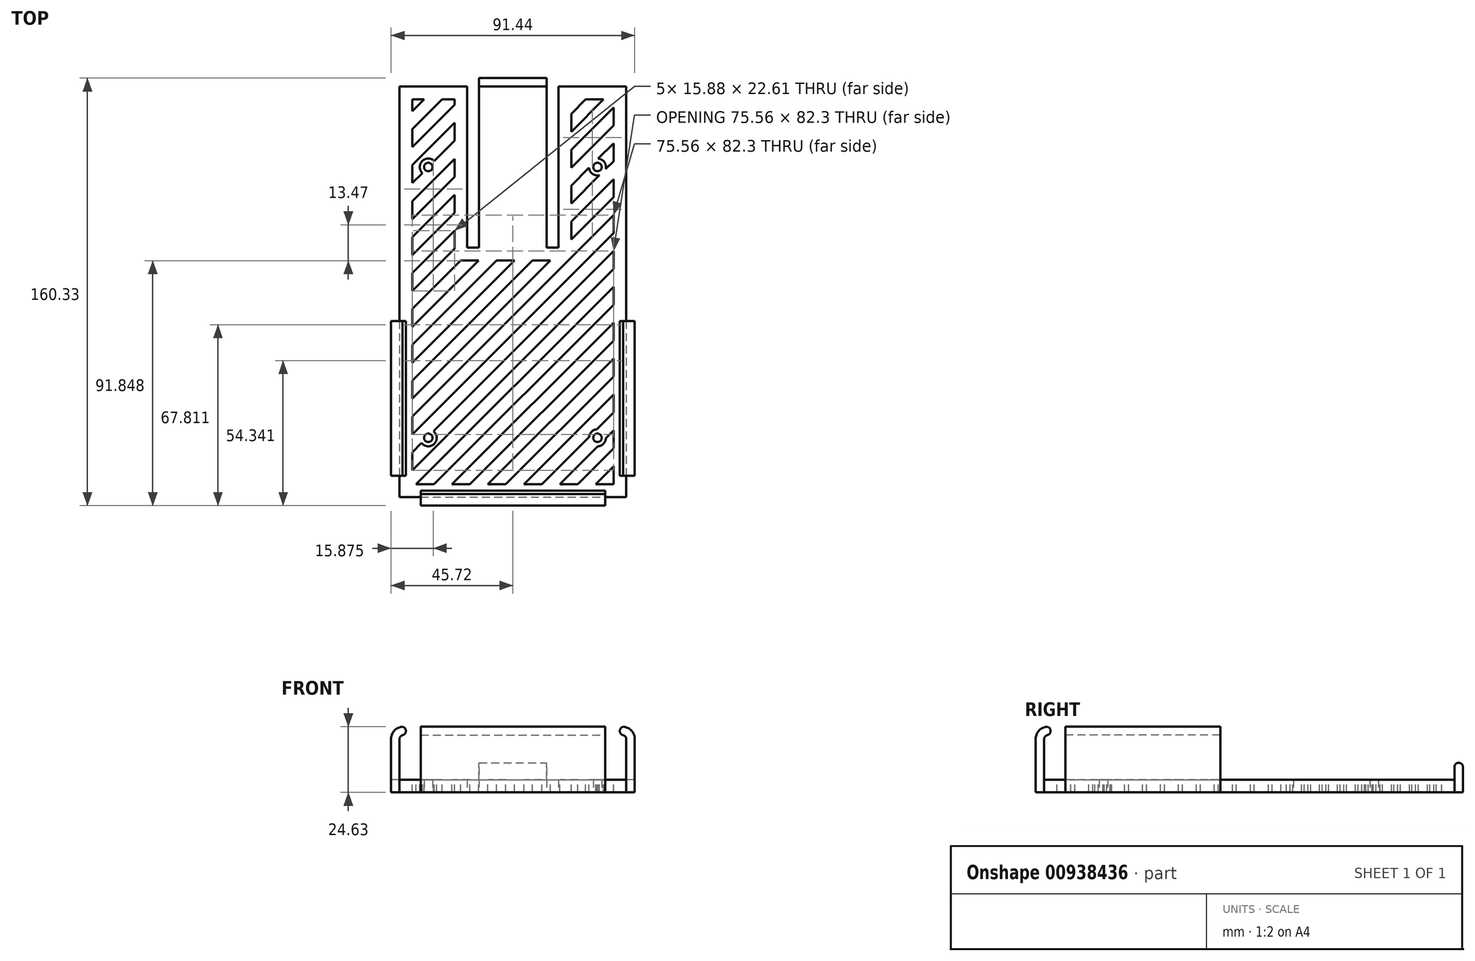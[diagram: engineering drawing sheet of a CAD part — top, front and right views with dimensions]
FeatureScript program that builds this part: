
annotation { "Feature Type Name" : "Feature", "Feature Type Description" : "" }
export const myFeature = defineFeature(function(context is Context, id is Id, definition is map)
    precondition{}
    {
        {
            var Q0;
            Q0=qCreatedBy(makeId("Top.planeOp"),FACE);
            var sketch = newSketch(context, id + "F0", { "sketchPlane" : qUnion([Q0])});
            skLineSegment(sketch, "E0.bottom", {"start": v(-42.54, 87.9) * mm, "end": v(-17.14, 87.9) * mm});
            skLineSegment(sketch, "E0.left", {"start": v(-42.54, 87.9) * mm, "end": v(-42.55, 0) * mm});
            skLineSegment(sketch, "E0.right", {"start": v(42.55, 87.9) * mm, "end": v(42.55, 0) * mm});
            skLineSegment(sketch, "E1", {"start": v(-42.55, 0) * mm, "end": v(-45.72, 0) * mm});
            skLineSegment(sketch, "E2", {"start": v(-45.72, 0) * mm, "end": v(-45.72, -58.15) * mm});
            skLineSegment(sketch, "E3", {"start": v(-45.72, -58.15) * mm, "end": v(-42.54, -58.15) * mm});
            skLineSegment(sketch, "E4", {"start": v(-34.6, -66.09) * mm, "end": v(-34.6, -69.26) * mm});
            skLineSegment(sketch, "E5", {"start": v(-34.6, -69.26) * mm, "end": v(34.6, -69.26) * mm});
            skLineSegment(sketch, "E6", {"start": v(34.6, -69.26) * mm, "end": v(34.6, -66.09) * mm});
            skLineSegment(sketch, "E7", {"start": v(42.54, -58.15) * mm, "end": v(45.72, -58.15) * mm});
            skLineSegment(sketch, "E8", {"start": v(45.72, -58.15) * mm, "end": v(45.72, 0) * mm});
            skLineSegment(sketch, "E9", {"start": v(45.72, 0) * mm, "end": v(42.55, 0) * mm});
            skLineSegment(sketch, "E10", {"start": v(-17.14, 87.9) * mm, "end": v(-17.15, 27.49) * mm});
            skLineSegment(sketch, "E11", {"start": v(-17.15, 27.49) * mm, "end": v(-12.7, 27.49) * mm});
            skLineSegment(sketch, "E12", {"start": v(17.15, 27.49) * mm, "end": v(17.15, 87.9) * mm});
            skLineSegment(sketch, "E13.trimOffspring", {"start": v(17.14, 87.9) * mm, "end": v(42.54, 87.9) * mm});
            skLineSegment(sketch, "E14", {"start": v(-12.7, 27.49) * mm, "end": v(-12.7, 91.07) * mm});
            skLineSegment(sketch, "E15", {"start": v(-12.7, 91.07) * mm, "end": v(12.7, 91.07) * mm});
            skLineSegment(sketch, "E16", {"start": v(12.7, 91.07) * mm, "end": v(12.7, 27.49) * mm});
            skLineSegment(sketch, "E17.trimOffspring", {"start": v(12.7, 27.49) * mm, "end": v(17.15, 27.49) * mm});
            skCircle(sketch, "E18", {"center": v(-31.75, -43.86) * mm, "radius": 1.59 * mm});
            skCircle(sketch, "E19", {"center": v(31.75, -43.86) * mm, "radius": 1.59 * mm});
            skCircle(sketch, "E20", {"center": v(31.75, 57.74) * mm, "radius": 1.59 * mm});
            skCircle(sketch, "E21", {"center": v(-31.75, 57.74) * mm, "radius": 1.59 * mm});
            skLineSegment(sketch, "E22", {"start": v(-42.54, -58.15) * mm, "end": v(-42.54, -66.09) * mm});
            skLineSegment(sketch, "E23", {"start": v(-42.54, -66.09) * mm, "end": v(-34.6, -66.09) * mm});
            skLineSegment(sketch, "E24", {"start": v(42.54, -58.15) * mm, "end": v(42.54, -66.09) * mm});
            skLineSegment(sketch, "E25", {"start": v(42.54, -66.09) * mm, "end": v(34.6, -66.09) * mm});
            skSolve(sketch);
        }
        {
            var Q0;
            Q0=qSketchRegion(id+"F0",true);
            extrude(context, id + "F1", {"entities" : qUnion([Q0]), "depth" : 4.76 * mm, "offsetDistance" : 25.4 * mm});
        }
        {
            var Q0;
            Q0=makeQuery(id+"F1.opExtrude","SWEPT_FACE",FACE,{"disambiguationData":[OSD([sQuery(id+"F0.wireOp",EDGE,"E3")])]});
            var sketch = newSketch(context, id + "F2", { "sketchPlane" : qUnion([Q0])});
            skLineSegment(sketch, "E26", {"start": v(0, 0) * mm, "end": v(0, 29.09) * mm, "construction": true});
            skLineSegment(sketch, "E27", {"start": v(-45.72, 4.76) * mm, "end": v(-45.72, 4.76) * mm});
            skLineSegment(sketch, "E28", {"start": v(45.72, 4.76) * mm, "end": v(45.72, 4.76) * mm});
            skPoint(sketch, "E29.end.orphan", {"position": v(-45.72, 20) * mm});
            skPoint(sketch, "E30.MirrorCS.end.orphan", {"position": v(45.72, 20) * mm});
            skLineSegment(sketch, "E31", {"start": v(-45.72, 4.76) * mm, "end": v(-45.72, 20) * mm});
            skLineSegment(sketch, "E32", {"start": v(-42.54, 4.76) * mm, "end": v(-42.54, 20) * mm});
            skArc(sketch, "E33", {"start": v(-41.4, 24.63) * mm, "mid": v(-44.49, 23.18) * mm, "end": v(-45.72, 20) * mm});
            skArc(sketch, "E34", {"start": v(-41.4, 21.46) * mm, "mid": v(-42.23, 20.93) * mm, "end": v(-42.54, 20) * mm});
            skArc(sketch, "E35", {"start": v(-41.4, 21.46) * mm, "mid": v(-40.13, 23.05) * mm, "end": v(-41.4, 24.63) * mm});
            skLineSegment(sketch, "E36", {"start": v(-45.72, 4.76) * mm, "end": v(-42.54, 4.76) * mm});
            skLineSegment(sketch, "E37.MirrorCS", {"start": v(42.54, 4.76) * mm, "end": v(42.54, 20) * mm});
            skLineSegment(sketch, "E38.MirrorCS", {"start": v(45.72, 4.76) * mm, "end": v(45.72, 20) * mm});
            skArc(sketch, "E39.MirrorCS", {"start": v(41.4, 24.63) * mm, "mid": v(44.49, 23.18) * mm, "end": v(45.72, 20) * mm});
            skArc(sketch, "E40.MirrorCS", {"start": v(41.4, 21.46) * mm, "mid": v(42.23, 20.93) * mm, "end": v(42.54, 20) * mm});
            skArc(sketch, "E41.MirrorCS", {"start": v(41.4, 21.46) * mm, "mid": v(40.13, 23.05) * mm, "end": v(41.4, 24.63) * mm});
            skLineSegment(sketch, "E42", {"start": v(45.72, 4.76) * mm, "end": v(42.54, 4.76) * mm});
            skSolve(sketch);
        }
        {
            var Q0;
            Q0=qSketchRegion(id+"F2",true);
            extrude(context, id + "F3", {"entities" : qUnion([Q0]), "operationType" : NewBodyOperationType.ADD, "oppositeDirection" : true, "depth" : 58.14 * mm, "offsetDistance" : 25.4 * mm});
        }
        {
            var Q0;
            Q0=makeQuery(id+"F1.opExtrude","SWEPT_FACE",FACE,{"disambiguationData":[OSD([sQuery(id+"F0.wireOp",EDGE,"E6")])]});
            var sketch = newSketch(context, id + "F4", { "sketchPlane" : qUnion([Q0])});
            skLineSegment(sketch, "E43", {"start": v(-69.26, 4.76) * mm, "end": v(-69.26, 4.76) * mm});
            skLineSegment(sketch, "E44", {"start": v(-69.26, 4.76) * mm, "end": v(-69.26, 20) * mm});
            skLineSegment(sketch, "E45", {"start": v(-66.09, 4.76) * mm, "end": v(-66.09, 20) * mm});
            skArc(sketch, "E46", {"start": v(-64.95, 21.46) * mm, "mid": v(-65.77, 20.93) * mm, "end": v(-66.09, 20) * mm});
            skArc(sketch, "E47", {"start": v(-64.95, 24.63) * mm, "mid": v(-68.03, 23.18) * mm, "end": v(-69.26, 20) * mm});
            skArc(sketch, "E48", {"start": v(-64.95, 21.46) * mm, "mid": v(-63.67, 23.05) * mm, "end": v(-64.95, 24.63) * mm});
            skLineSegment(sketch, "E49", {"start": v(-69.26, 4.76) * mm, "end": v(-66.09, 4.76) * mm});
            skSolve(sketch);
        }
        {
            var Q0;
            Q0=qSketchRegion(id+"F4",true);
            extrude(context, id + "F5", {"entities" : qUnion([Q0]), "operationType" : NewBodyOperationType.ADD, "oppositeDirection" : true, "depth" : 69.22 * mm, "offsetDistance" : 25.4 * mm});
        }
        {
            var Q0;
            Q0=makeQuery(id+"F1.opExtrude","SWEPT_FACE",FACE,{"disambiguationData":[OSD([sQuery(id+"F0.wireOp",EDGE,"E16")])]});
            var sketch = newSketch(context, id + "F6", { "sketchPlane" : qUnion([Q0])});
            skLineSegment(sketch, "E50", {"start": v(91.07, 4.76) * mm, "end": v(91.07, 9.54) * mm});
            skLineSegment(sketch, "E51", {"start": v(87.9, 4.76) * mm, "end": v(87.9, 9.54) * mm});
            skArc(sketch, "E52", {"start": v(91.07, 9.54) * mm, "mid": v(89.49, 11.13) * mm, "end": v(87.9, 9.54) * mm});
            skLineSegment(sketch, "E53", {"start": v(87.9, 4.76) * mm, "end": v(91.07, 4.76) * mm});
            skSolve(sketch);
        }
        {
            var Q0;
            Q0=qSketchRegion(id+"F6",true);
            extrude(context, id + "F7", {"entities" : qUnion([Q0]), "operationType" : NewBodyOperationType.ADD, "oppositeDirection" : true, "depth" : 25.4 * mm, "offsetDistance" : 25.4 * mm});
        }
        {
            var Q0;
            Q0=makeQuery(id+"F1.opExtrude","CAP_FACE",FACE,{"disambiguationData":[OSD([sQuery(id+"F0.wireOp",EDGE,"E0.bottom"),sQuery(id+"F0.wireOp",EDGE,"E0.left"),sQuery(id+"F0.wireOp",EDGE,"E0.right"),sQuery(id+"F0.wireOp",EDGE,"E1"),sQuery(id+"F0.wireOp",EDGE,"E2"),sQuery(id+"F0.wireOp",EDGE,"E3"),sQuery(id+"F0.wireOp",EDGE,"E4"),sQuery(id+"F0.wireOp",EDGE,"E5"),sQuery(id+"F0.wireOp",EDGE,"E6"),sQuery(id+"F0.wireOp",EDGE,"E7"),sQuery(id+"F0.wireOp",EDGE,"E8"),sQuery(id+"F0.wireOp",EDGE,"E9"),sQuery(id+"F0.wireOp",EDGE,"E10"),sQuery(id+"F0.wireOp",EDGE,"E11"),sQuery(id+"F0.wireOp",EDGE,"E12"),sQuery(id+"F0.wireOp",EDGE,"E13.trimOffspring"),sQuery(id+"F0.wireOp",EDGE,"E14"),sQuery(id+"F0.wireOp",EDGE,"E15"),sQuery(id+"F0.wireOp",EDGE,"E16"),sQuery(id+"F0.wireOp",EDGE,"E17.trimOffspring"),sQuery(id+"F0.wireOp",EDGE,"E18"),sQuery(id+"F0.wireOp",EDGE,"E19"),sQuery(id+"F0.wireOp",EDGE,"E20"),sQuery(id+"F0.wireOp",EDGE,"E21"),sQuery(id+"F0.wireOp",EDGE,"E22"),sQuery(id+"F0.wireOp",EDGE,"E23"),sQuery(id+"F0.wireOp",EDGE,"E24"),sQuery(id+"F0.wireOp",EDGE,"E25")])],"isStart":false});
            var sketch = newSketch(context, id + "F8", { "sketchPlane" : qUnion([Q0])});
            skLineSegment(sketch, "E54", {"start": v(-37.78, 83.14) * mm, "end": v(-33.28, 83.14) * mm});
            skLineSegment(sketch, "E55", {"start": v(-21.9, 83.14) * mm, "end": v(-21.9, 81.04) * mm});
            skLineSegment(sketch, "E56", {"start": v(-19.6, 22.73) * mm, "end": v(-12.87, 22.73) * mm});
            skLineSegment(sketch, "E57", {"start": v(27.34, 83.14) * mm, "end": v(34.07, 83.14) * mm});
            skLineSegment(sketch, "E58", {"start": v(37.78, 80.11) * mm, "end": v(37.78, 73.38) * mm});
            skLineSegment(sketch, "E59", {"start": v(37.78, -61.33) * mm, "end": v(31.05, -61.33) * mm});
            skLineSegment(sketch, "E60", {"start": v(-37.78, -56.07) * mm, "end": v(-37.78, -49.33) * mm});
            skArc(sketch, "E61", {"start": v(-34.26, -45.81) * mm, "mid": v(-29.5, -46.1) * mm, "end": v(-29.8, -41.36) * mm});
            skArc(sketch, "E62", {"start": v(28.59, 57.45) * mm, "mid": v(29.92, 55.14) * mm, "end": v(32.54, 54.66) * mm});
            skArc(sketch, "E63", {"start": v(-29.5, 59.98) * mm, "mid": v(-34, 59.98) * mm, "end": v(-34, 55.49) * mm});
            skLineSegment(sketch, "E64", {"start": v(31.05, -61.33) * mm, "end": v(37.78, -54.6) * mm});
            skLineSegment(sketch, "E65", {"start": v(24.31, -61.33) * mm, "end": v(37.78, -47.86) * mm});
            skLineSegment(sketch, "E66", {"start": v(17.58, -61.33) * mm, "end": v(31.87, -47.04) * mm});
            skLineSegment(sketch, "E67", {"start": v(10.84, -61.33) * mm, "end": v(28.59, -43.58) * mm});
            skLineSegment(sketch, "E68.trimOffspring", {"start": v(34.92, -43.98) * mm, "end": v(37.78, -41.12) * mm});
            skLineSegment(sketch, "E69.trimOffspring", {"start": v(31.47, -40.7) * mm, "end": v(37.78, -34.39) * mm});
            skLineSegment(sketch, "E70.trimOffspring", {"start": v(24.31, -61.33) * mm, "end": v(17.58, -61.33) * mm});
            skLineSegment(sketch, "E71.trimOffspring", {"start": v(37.78, -54.6) * mm, "end": v(37.78, -61.33) * mm});
            skLineSegment(sketch, "E72.trimOffspring", {"start": v(10.84, -61.33) * mm, "end": v(4.1, -61.33) * mm});
            skLineSegment(sketch, "E73.trimOffspring", {"start": v(37.78, -41.12) * mm, "end": v(37.78, -47.86) * mm});
            skPoint(sketch, "E74.center.orphan", {"position": v(31.75, -43.86) * mm});
            skArc(sketch, "E75", {"start": v(31.87, -47.04) * mm, "mid": v(34, -46.1) * mm, "end": v(34.92, -43.98) * mm});
            skArc(sketch, "E76.trimOffspring", {"start": v(31.47, -40.7) * mm, "mid": v(29.5, -41.62) * mm, "end": v(28.59, -43.58) * mm});
            skLineSegment(sketch, "E77", {"start": v(4.1, -61.33) * mm, "end": v(37.78, -27.65) * mm});
            skLineSegment(sketch, "E78", {"start": v(-2.63, -61.33) * mm, "end": v(37.78, -20.92) * mm});
            skLineSegment(sketch, "E79", {"start": v(-9.36, -61.33) * mm, "end": v(37.78, -14.18) * mm});
            skLineSegment(sketch, "E80", {"start": v(-16.1, -61.33) * mm, "end": v(37.78, -7.45) * mm});
            skLineSegment(sketch, "E81", {"start": v(-22.83, -61.33) * mm, "end": v(37.78, -0.7) * mm});
            skLineSegment(sketch, "E82.trimOffspring", {"start": v(-2.63, -61.33) * mm, "end": v(-9.36, -61.33) * mm});
            skLineSegment(sketch, "E83.trimOffspring", {"start": v(-16.1, -61.33) * mm, "end": v(-22.83, -61.33) * mm});
            skLineSegment(sketch, "E84.trimOffspring", {"start": v(37.78, -27.65) * mm, "end": v(37.78, -34.39) * mm});
            skLineSegment(sketch, "E85.trimOffspring", {"start": v(37.78, -14.18) * mm, "end": v(37.78, -20.92) * mm});
            skLineSegment(sketch, "E86", {"start": v(-29.57, -61.33) * mm, "end": v(37.78, 6.03) * mm});
            skLineSegment(sketch, "E87", {"start": v(-36.3, -61.33) * mm, "end": v(37.78, 12.76) * mm});
            skLineSegment(sketch, "E88", {"start": v(-37.78, -56.07) * mm, "end": v(37.78, 19.5) * mm});
            skLineSegment(sketch, "E89", {"start": v(-37.78, -49.33) * mm, "end": v(-34.26, -45.81) * mm});
            skLineSegment(sketch, "E90", {"start": v(-37.78, -42.6) * mm, "end": v(37.78, 32.97) * mm});
            skLineSegment(sketch, "E91", {"start": v(-37.78, -35.86) * mm, "end": v(20.8, 22.73) * mm});
            skLineSegment(sketch, "E92", {"start": v(-37.78, -29.13) * mm, "end": v(14.07, 22.73) * mm});
            skLineSegment(sketch, "E93", {"start": v(-37.78, -22.4) * mm, "end": v(7.34, 22.73) * mm});
            skLineSegment(sketch, "E94", {"start": v(-37.78, -15.66) * mm, "end": v(0.6, 22.73) * mm});
            skLineSegment(sketch, "E95", {"start": v(-37.78, -8.92) * mm, "end": v(-6.13, 22.73) * mm});
            skLineSegment(sketch, "E96", {"start": v(-37.78, -2.19) * mm, "end": v(-12.87, 22.73) * mm});
            skLineSegment(sketch, "E97", {"start": v(-37.78, 4.55) * mm, "end": v(-19.6, 22.73) * mm});
            skLineSegment(sketch, "E98", {"start": v(-37.78, 11.28) * mm, "end": v(-21.9, 27.16) * mm});
            skLineSegment(sketch, "E99", {"start": v(-37.78, 18.02) * mm, "end": v(-21.9, 33.9) * mm});
            skLineSegment(sketch, "E100", {"start": v(-37.78, 24.75) * mm, "end": v(-21.9, 40.63) * mm});
            skLineSegment(sketch, "E101", {"start": v(-37.78, 31.49) * mm, "end": v(-21.9, 47.36) * mm});
            skLineSegment(sketch, "E102", {"start": v(-37.78, 38.22) * mm, "end": v(-21.9, 54.1) * mm});
            skLineSegment(sketch, "E103", {"start": v(-37.78, 44.96) * mm, "end": v(-21.9, 60.83) * mm});
            skLineSegment(sketch, "E104", {"start": v(-37.78, 51.7) * mm, "end": v(-34, 55.49) * mm});
            skLineSegment(sketch, "E105", {"start": v(-37.78, 58.43) * mm, "end": v(-21.9, 74.3) * mm});
            skLineSegment(sketch, "E106", {"start": v(-37.78, 65.16) * mm, "end": v(-21.9, 81.04) * mm});
            skLineSegment(sketch, "E107", {"start": v(-26.55, 83.14) * mm, "end": v(-37.78, 71.9) * mm});
            skLineSegment(sketch, "E108.trimOffspring", {"start": v(-29.57, -61.33) * mm, "end": v(-36.3, -61.33) * mm});
            skLineSegment(sketch, "E109.trimOffspring", {"start": v(-37.78, -42.6) * mm, "end": v(-37.78, -35.86) * mm});
            skLineSegment(sketch, "E110.trimOffspring", {"start": v(-37.78, -29.13) * mm, "end": v(-37.78, -22.4) * mm});
            skLineSegment(sketch, "E111.trimOffspring", {"start": v(-37.78, -15.66) * mm, "end": v(-37.78, -8.92) * mm});
            skLineSegment(sketch, "E112.trimOffspring", {"start": v(-37.78, -2.19) * mm, "end": v(-37.78, 4.55) * mm});
            skLineSegment(sketch, "E113.trimOffspring", {"start": v(-37.78, 11.28) * mm, "end": v(-37.78, 18.02) * mm});
            skLineSegment(sketch, "E114.trimOffspring", {"start": v(-37.78, 24.75) * mm, "end": v(-37.78, 31.49) * mm});
            skLineSegment(sketch, "E115.trimOffspring", {"start": v(-37.78, 38.22) * mm, "end": v(-37.78, 44.96) * mm});
            skLineSegment(sketch, "E116.trimOffspring", {"start": v(-37.78, 51.7) * mm, "end": v(-37.78, 58.43) * mm});
            skLineSegment(sketch, "E117.trimOffspring", {"start": v(-37.78, 65.16) * mm, "end": v(-37.78, 71.9) * mm});
            skLineSegment(sketch, "E118.trimOffspring", {"start": v(37.78, -0.7) * mm, "end": v(37.78, -7.45) * mm});
            skLineSegment(sketch, "E119.trimOffspring", {"start": v(37.78, 12.76) * mm, "end": v(37.78, 6.03) * mm});
            skLineSegment(sketch, "E120.trimOffspring", {"start": v(37.78, 26.23) * mm, "end": v(37.78, 19.5) * mm});
            skLineSegment(sketch, "E121.trimOffspring", {"start": v(37.78, 39.7) * mm, "end": v(37.78, 32.97) * mm});
            skLineSegment(sketch, "E122.trimOffspring", {"start": v(37.78, 53.17) * mm, "end": v(37.78, 46.44) * mm});
            skLineSegment(sketch, "E123.trimOffspring", {"start": v(37.78, 66.64) * mm, "end": v(37.78, 59.9) * mm});
            skLineSegment(sketch, "E124.trimOffspring", {"start": v(21.9, 77.7) * mm, "end": v(27.34, 83.14) * mm});
            skLineSegment(sketch, "E125.trimOffspring", {"start": v(21.9, 70.97) * mm, "end": v(34.07, 83.14) * mm});
            skLineSegment(sketch, "E126.trimOffspring", {"start": v(21.9, 64.24) * mm, "end": v(37.78, 80.11) * mm});
            skLineSegment(sketch, "E127.trimOffspring", {"start": v(21.9, 57.5) * mm, "end": v(37.78, 73.38) * mm});
            skLineSegment(sketch, "E128.trimOffspring", {"start": v(21.9, 50.77) * mm, "end": v(28.59, 57.45) * mm});
            skLineSegment(sketch, "E129.trimOffspring", {"start": v(21.9, 44.03) * mm, "end": v(32.54, 54.66) * mm});
            skLineSegment(sketch, "E130.trimOffspring", {"start": v(21.9, 37.3) * mm, "end": v(37.78, 53.17) * mm});
            skLineSegment(sketch, "E131.trimOffspring", {"start": v(21.9, 30.56) * mm, "end": v(37.78, 46.44) * mm});
            skLineSegment(sketch, "E132.trimOffspring", {"start": v(21.9, 70.97) * mm, "end": v(21.9, 77.7) * mm});
            skLineSegment(sketch, "E133.trimOffspring", {"start": v(21.9, 57.5) * mm, "end": v(21.9, 64.24) * mm});
            skLineSegment(sketch, "E134.trimOffspring", {"start": v(21.9, 44.03) * mm, "end": v(21.9, 50.77) * mm});
            skLineSegment(sketch, "E135.trimOffspring", {"start": v(21.9, 30.56) * mm, "end": v(21.9, 37.3) * mm});
            skLineSegment(sketch, "E136.trimOffspring", {"start": v(20.8, 22.73) * mm, "end": v(37.78, 39.7) * mm});
            skLineSegment(sketch, "E137.trimOffspring", {"start": v(7.34, 22.73) * mm, "end": v(14.07, 22.73) * mm});
            skLineSegment(sketch, "E138.trimOffspring", {"start": v(-6.13, 22.73) * mm, "end": v(0.6, 22.73) * mm});
            skLineSegment(sketch, "E139.trimOffspring", {"start": v(-21.9, 33.9) * mm, "end": v(-21.9, 27.16) * mm});
            skLineSegment(sketch, "E140.trimOffspring", {"start": v(-21.9, 47.36) * mm, "end": v(-21.9, 40.63) * mm});
            skLineSegment(sketch, "E141.trimOffspring", {"start": v(-21.9, 60.83) * mm, "end": v(-21.9, 54.1) * mm});
            skLineSegment(sketch, "E142.trimOffspring", {"start": v(-21.9, 74.3) * mm, "end": v(-21.9, 67.57) * mm});
            skLineSegment(sketch, "E143", {"start": v(-37.78, 78.63) * mm, "end": v(-33.28, 83.14) * mm});
            skLineSegment(sketch, "E144.trimOffspring", {"start": v(-37.78, 78.63) * mm, "end": v(-37.78, 83.14) * mm});
            skLineSegment(sketch, "E145.trimOffspring", {"start": v(-26.55, 83.14) * mm, "end": v(-21.9, 83.14) * mm});
            skLineSegment(sketch, "E146.trimOffspring", {"start": v(-29.5, 59.98) * mm, "end": v(-21.9, 67.57) * mm});
            skLineSegment(sketch, "E147.trimOffspring", {"start": v(32.04, 60.9) * mm, "end": v(37.78, 66.64) * mm});
            skArc(sketch, "E148.trimOffspring", {"start": v(34.83, 56.95) * mm, "mid": v(34.34, 59.57) * mm, "end": v(32.04, 60.9) * mm});
            skLineSegment(sketch, "E149.trimOffspring", {"start": v(34.83, 56.95) * mm, "end": v(37.78, 59.9) * mm});
            skLineSegment(sketch, "E150.trimOffspring", {"start": v(-29.8, -41.36) * mm, "end": v(37.78, 26.23) * mm});
            skLineSegment(sketch, "E151", {"start": v(20.8, 22.73) * mm, "end": v(20.8, 22.73) * mm});
            skSolve(sketch);
        }
        {
            var Q0;
            Q0 = qSketchRegion(id + "F8", true);
            extrude(context, id + "F9", {"entities" : qUnion([Q0]), "operationType" : NewBodyOperationType.REMOVE, "oppositeDirection" : true, "depth" : 4.76 * mm, "offsetDistance" : 25.4 * mm});
        }
    });
